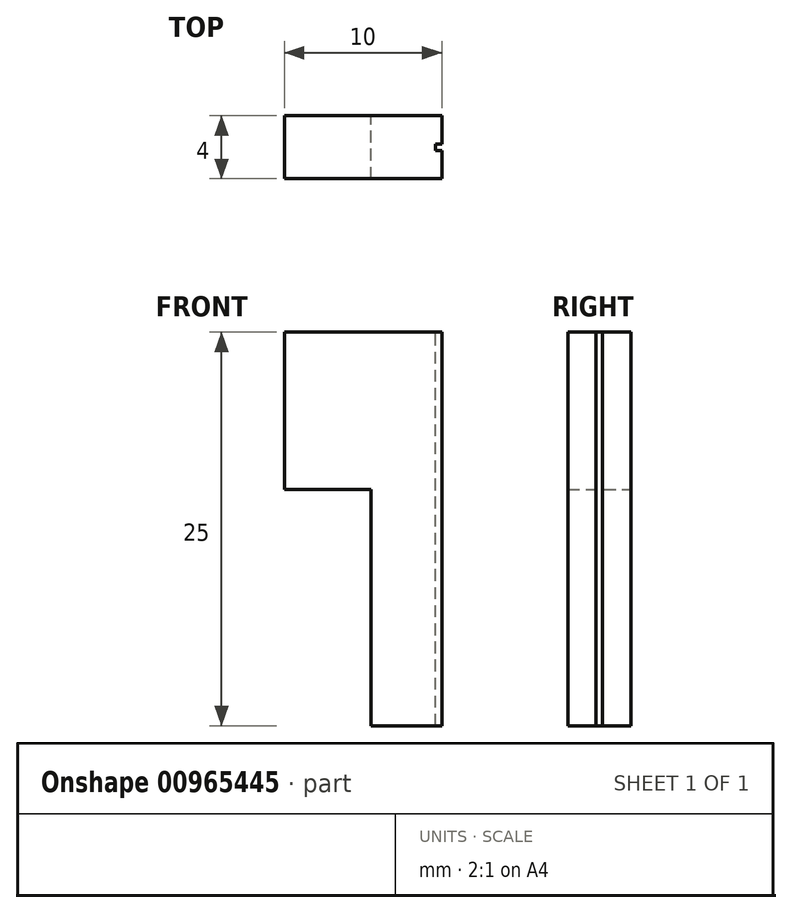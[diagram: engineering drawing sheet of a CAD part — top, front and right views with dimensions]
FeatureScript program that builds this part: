
annotation { "Feature Type Name" : "Feature", "Feature Type Description" : "" }
export const myFeature = defineFeature(function(context is Context, id is Id, definition is map)
    precondition{}
    {
        {
            var Q0;
            Q0=qCreatedBy(makeId("Front.planeOp"),FACE);
            var sketch = newSketch(context, id + "F0", { "sketchPlane" : qUnion([Q0])});
            skLineSegment(sketch, "E0.bottom", {"start": v(10.93, 5.85) * mm, "end": v(2.93, 5.85) * mm});
            skLineSegment(sketch, "E0.top", {"start": v(10.93, -4.15) * mm, "end": v(5.43, -4.15) * mm});
            skLineSegment(sketch, "E0.left", {"start": v(10.93, 5.85) * mm, "end": v(10.93, -4.15) * mm});
            skLineSegment(sketch, "E0.right", {"start": v(-9.07, 5.85) * mm, "end": v(-9.07, -4.15) * mm});
            skPoint(sketch, "E0.middle", {"position": v(0.93, 0.85) * mm});
            skPoint(sketch, "E1.middle", {"position": v(0.93, 5.85) * mm});
            skLineSegment(sketch, "E2.top", {"start": v(5.43, -19.15) * mm, "end": v(-3.57, -19.15) * mm});
            skLineSegment(sketch, "E2.left", {"start": v(5.43, -4.15) * mm, "end": v(5.43, -19.15) * mm});
            skLineSegment(sketch, "E2.right", {"start": v(-3.57, -4.15) * mm, "end": v(-3.57, -19.15) * mm});
            skPoint(sketch, "E2.middle", {"position": v(0.93, -11.65) * mm});
            skPoint(sketch, "E2.middle.positionSnap0", {"position": v(0.93, -4.15) * mm});
            skPoint(sketch, "E2.centerSnap0", {"position": v(0.93, -4.15) * mm});
            skPoint(sketch, "E3.orphan", {"position": v(2.93, -24.15) * mm});
            skPoint(sketch, "E4.orphan", {"position": v(-1.07, -24.15) * mm});
            skLineSegment(sketch, "E5.trimOffspring", {"start": v(-3.57, -4.15) * mm, "end": v(-9.07, -4.15) * mm});
            skLineSegment(sketch, "E6.trimOffspring", {"start": v(-1.07, 5.85) * mm, "end": v(-9.07, 5.85) * mm});
            skLineSegment(sketch, "E7", {"start": v(-1.07, 5.85) * mm, "end": v(2.93, 5.85) * mm});
            skSolve(sketch);
        }
        {
            var Q0;
            Q0 = qSketchRegion(id + "F0", true);
            extrude(context, id + "F1", {"entities" : qUnion([Q0]), "depth" : 4 * mm, "offsetDistance" : 25 * mm});
        }
        {
            var Q0;
            Q0=makeQuery(id+"F1.opExtrude","SWEPT_FACE",FACE,{"disambiguationData":[OSD([sQuery(id+"F0.wireOp",EDGE,"E0.bottom"),sQuery(id+"F0.wireOp",EDGE,"E6.trimOffspring"),sQuery(id+"F0.wireOp",EDGE,"E7")])]});
            var sketch = newSketch(context, id + "F2", { "sketchPlane" : qUnion([Q0])});
            skLineSegment(sketch, "E8.bottom", {"start": v(10.93, 0) * mm, "end": v(0.93, 0) * mm});
            skLineSegment(sketch, "E8.top", {"start": v(10.93, -4) * mm, "end": v(0.93, -4) * mm});
            skLineSegment(sketch, "E8.left", {"start": v(10.93, 0) * mm, "end": v(10.93, -4) * mm});
            skLineSegment(sketch, "E8.right", {"start": v(0.93, 0) * mm, "end": v(0.93, -1.8) * mm});
            skPoint(sketch, "E8.middle", {"position": v(5.93, -2) * mm});
            skPoint(sketch, "E8.middle.positionSnap0", {"position": v(10.93, -2) * mm});
            skPoint(sketch, "E8.centerSnap0", {"position": v(10.93, -2) * mm});
            skLineSegment(sketch, "E9.bottom", {"start": v(0.53, -2.2) * mm, "end": v(0.93, -2.2) * mm});
            skLineSegment(sketch, "E9.top", {"start": v(0.53, -1.8) * mm, "end": v(0.93, -1.8) * mm});
            skLineSegment(sketch, "E9.left", {"start": v(0.53, -2.2) * mm, "end": v(0.53, -1.8) * mm});
            skPoint(sketch, "E9.middle", {"position": v(0.93, -2) * mm});
            skLineSegment(sketch, "E10.trimOffspring", {"start": v(0.93, -2.2) * mm, "end": v(0.93, -4) * mm});
            skPoint(sketch, "E9.right.end.orphan", {"position": v(1.33, -1.8) * mm});
            skPoint(sketch, "E11.orphan", {"position": v(1.33, -2.2) * mm});
            skSolve(sketch);
        }
        {
            var Q0;
            Q0 = qSketchRegion(id + "F2", true);
            extrude(context, id + "F3", {"entities" : qUnion([Q0]), "operationType" : NewBodyOperationType.REMOVE, "oppositeDirection" : true, "depth" : 25 * mm, "offsetDistance" : 25 * mm});
        }
    });
